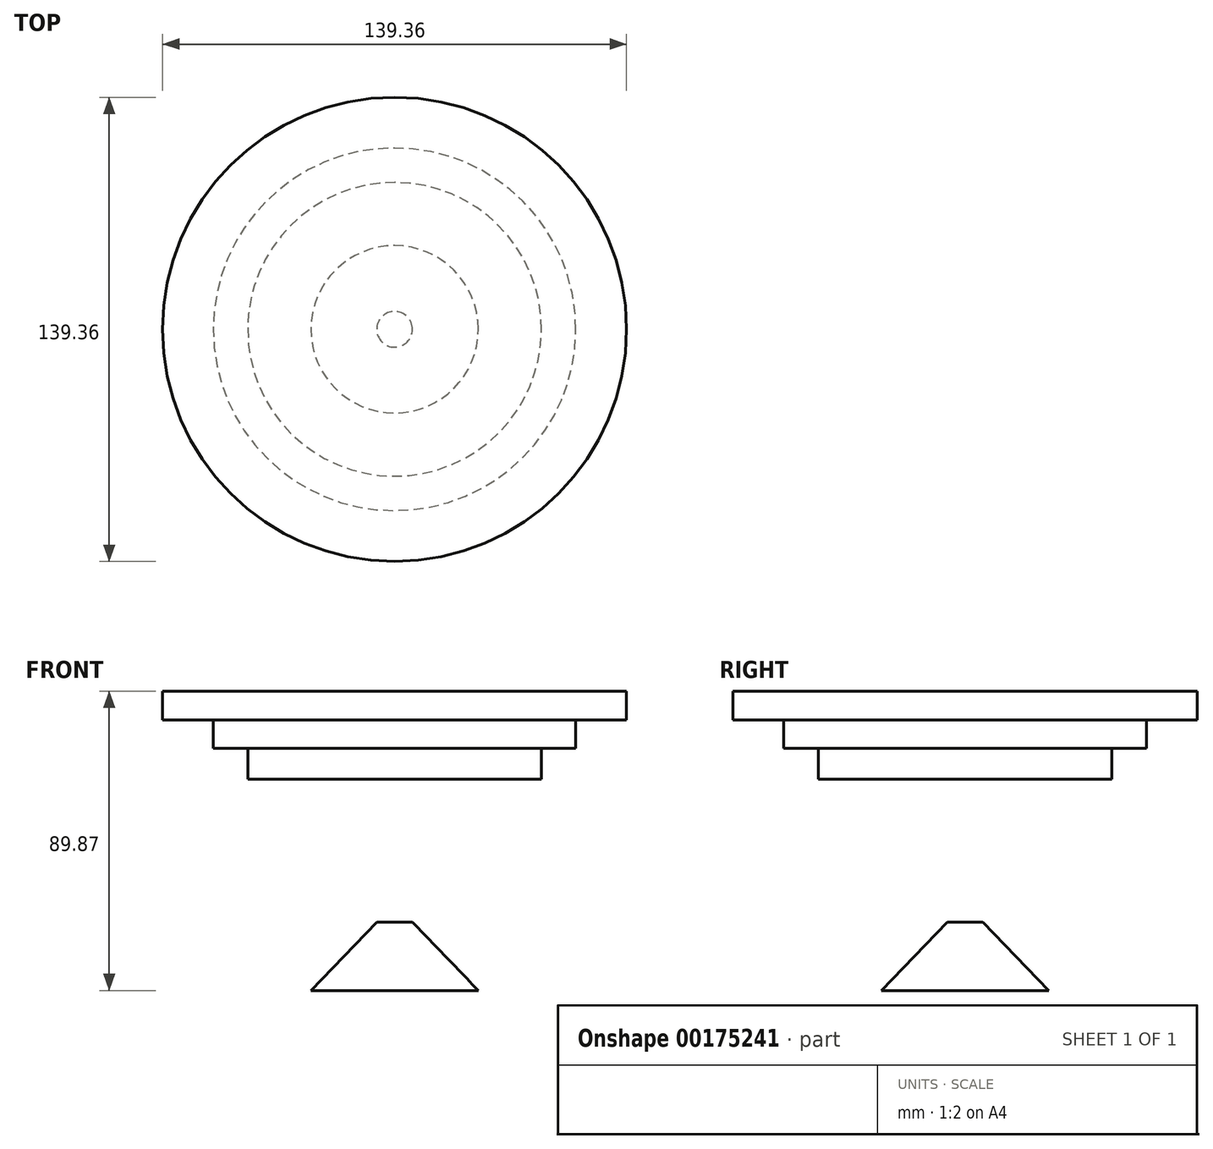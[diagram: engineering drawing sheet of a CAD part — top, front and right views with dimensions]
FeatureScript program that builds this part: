
annotation { "Feature Type Name" : "Feature", "Feature Type Description" : "" }
export const myFeature = defineFeature(function(context is Context, id is Id, definition is map)
    precondition{}
    {
        {
            var Q0;
            Q0=qCreatedBy(makeId("Front.planeOp"),FACE);
            var sketch = newSketch(context, id + "F0", { "sketchPlane" : qUnion([Q0])});
            skLineSegment(sketch, "E0", {"start": v(0, 69.58) * mm, "end": v(0, -55.57) * mm, "construction": true});
            skLineSegment(sketch, "E1", {"start": v(0, 40.38) * mm, "end": v(0, 31.14) * mm});
            skLineSegment(sketch, "E2", {"start": v(0, 31.14) * mm, "end": v(44.1, 31.14) * mm});
            skLineSegment(sketch, "E3", {"start": v(44.1, 31.14) * mm, "end": v(44.1, 40.38) * mm});
            skLineSegment(sketch, "E4.bottom", {"start": v(0, 31.14) * mm, "end": v(38.14, 31.14) * mm});
            skLineSegment(sketch, "E4.top", {"start": v(0, 22.5) * mm, "end": v(38.14, 22.5) * mm});
            skLineSegment(sketch, "E4.left", {"start": v(0, 31.14) * mm, "end": v(0, 22.5) * mm});
            skLineSegment(sketch, "E4.right", {"start": v(38.14, 31.14) * mm, "end": v(38.14, 22.5) * mm});
            skLineSegment(sketch, "E5.bottom", {"start": v(0, 22.5) * mm, "end": v(32.78, 22.5) * mm});
            skLineSegment(sketch, "E5.top", {"start": v(0, 15.94) * mm, "end": v(32.78, 15.94) * mm});
            skLineSegment(sketch, "E5.left", {"start": v(0, 22.5) * mm, "end": v(0, 15.94) * mm});
            skLineSegment(sketch, "E5.right", {"start": v(32.78, 22.5) * mm, "end": v(32.78, 15.94) * mm});
            skLineSegment(sketch, "E6.bottom", {"start": v(0, 15.94) * mm, "end": v(27.12, 15.94) * mm});
            skLineSegment(sketch, "E6.top", {"start": v(0, 9.98) * mm, "end": v(27.12, 9.98) * mm});
            skLineSegment(sketch, "E6.left", {"start": v(0, 15.94) * mm, "end": v(0, 9.98) * mm});
            skLineSegment(sketch, "E6.right", {"start": v(27.12, 15.94) * mm, "end": v(27.12, 9.98) * mm});
            skLineSegment(sketch, "E7.bottom", {"start": v(0, 9.98) * mm, "end": v(20.56, 9.98) * mm});
            skLineSegment(sketch, "E7.top", {"start": v(0, 4.62) * mm, "end": v(20.56, 4.62) * mm});
            skLineSegment(sketch, "E7.left", {"start": v(0, 9.98) * mm, "end": v(0, 4.62) * mm});
            skLineSegment(sketch, "E7.right", {"start": v(20.56, 9.98) * mm, "end": v(20.56, 4.62) * mm});
            skLineSegment(sketch, "E8.bottom", {"start": v(0, 4.62) * mm, "end": v(14.6, 4.62) * mm});
            skLineSegment(sketch, "E8.top", {"start": v(0, -2.53) * mm, "end": v(14.6, -2.53) * mm});
            skLineSegment(sketch, "E8.left", {"start": v(0, 4.62) * mm, "end": v(0, -2.53) * mm});
            skLineSegment(sketch, "E8.right", {"start": v(14.6, 4.62) * mm, "end": v(14.6, -2.53) * mm});
            skLineSegment(sketch, "E9.bottom", {"start": v(0, -2.53) * mm, "end": v(11.03, -2.53) * mm});
            skLineSegment(sketch, "E9.top", {"start": v(0, -6.7) * mm, "end": v(11.03, -6.7) * mm});
            skLineSegment(sketch, "E9.left", {"start": v(0, -2.53) * mm, "end": v(0, -6.7) * mm});
            skLineSegment(sketch, "E9.right", {"start": v(11.03, -2.53) * mm, "end": v(11.03, -6.7) * mm});
            skLineSegment(sketch, "E10.bottom", {"start": v(0, -6.7) * mm, "end": v(5.36, -6.7) * mm});
            skLineSegment(sketch, "E10.top", {"start": v(0, -11.77) * mm, "end": v(5.36, -11.77) * mm});
            skLineSegment(sketch, "E10.left", {"start": v(0, -6.7) * mm, "end": v(0, -11.77) * mm});
            skLineSegment(sketch, "E10.right", {"start": v(5.36, -6.7) * mm, "end": v(5.36, -11.77) * mm});
            skLineSegment(sketch, "E11.bottom", {"start": v(0, 40.38) * mm, "end": v(54.44, 40.38) * mm});
            skLineSegment(sketch, "E11.top", {"start": v(0, 48.88) * mm, "end": v(54.44, 48.88) * mm});
            skLineSegment(sketch, "E11.left", {"start": v(0, 40.38) * mm, "end": v(0, 48.88) * mm});
            skLineSegment(sketch, "E11.right", {"start": v(54.44, 40.38) * mm, "end": v(54.44, 48.88) * mm});
            skLineSegment(sketch, "E12.bottom", {"start": v(0, 48.88) * mm, "end": v(69.68, 48.88) * mm});
            skLineSegment(sketch, "E12.top", {"start": v(0, 57.56) * mm, "end": v(69.68, 57.56) * mm});
            skLineSegment(sketch, "E12.left", {"start": v(0, 48.88) * mm, "end": v(0, 57.56) * mm});
            skLineSegment(sketch, "E12.right", {"start": v(69.68, 48.88) * mm, "end": v(69.68, 57.56) * mm});
            skLineSegment(sketch, "E13", {"start": v(0, -11.77) * mm, "end": v(0, -32.3) * mm});
            skLineSegment(sketch, "E14", {"start": v(0, -32.3) * mm, "end": v(25.13, -32.3) * mm});
            skLineSegment(sketch, "E15", {"start": v(25.13, -32.3) * mm, "end": v(5.36, -11.77) * mm});
            skLineSegment(sketch, "E16", {"start": v(5.36, -11.77) * mm, "end": v(12.56, -32.3) * mm});
            skSolve(sketch);
        }
        {
            var Q0;
            Q0=makeQuery(id+"F0.imprint","IMPRINT",FACE,{"disambiguationData":[TD([[makeQuery(id+"F0.imprint","IMPRINT",EDGE,{"derivedFrom":sQuery(id+"F0.wireOp",EDGE,"E12.top")}),-1.0]])]});
            var Q1;
            {var subQ1=sQuery(id+"F0.wireOp",EDGE,"E11.left");Q1=makeQuery(id+"F0.imprint","IMPRINT",FACE,{"disambiguationData":[TD([[makeQuery(id+"F0.imprint","IMPRINT",EDGE,{"derivedFrom":subQ1}),-1.0]])]});}
            var Q2;
            {var subQ1=sQuery(id+"F0.wireOp",EDGE,"E1");Q2=makeQuery(id+"F0.imprint","IMPRINT",FACE,{"disambiguationData":[TD([[makeQuery(id+"F0.imprint","IMPRINT",EDGE,{"derivedFrom":subQ1}),1.0]])]});}
            var Q3;
            Q3=makeQuery(id+"F0.imprint","IMPRINT",FACE,{"disambiguationData":[TD([[makeQuery(id+"F0.imprint","IMPRINT",EDGE,{"derivedFrom":sQuery(id+"F0.wireOp",EDGE,"E4.bottom")}),-1.0]])]});
            var Q4;
            Q4=makeQuery(id+"F0.imprint","IMPRINT",FACE,{"disambiguationData":[TD([[makeQuery(id+"F0.imprint","IMPRINT",EDGE,{"derivedFrom":sQuery(id+"F0.wireOp",EDGE,"E5.bottom")}),-1.0]])]});
            var Q5;
            Q5=makeQuery(id+"F0.imprint","IMPRINT",FACE,{"disambiguationData":[TD([[makeQuery(id+"F0.imprint","IMPRINT",EDGE,{"derivedFrom":sQuery(id+"F0.wireOp",EDGE,"E6.bottom")}),-1.0]])]});
            var Q6;
            Q6=makeQuery(id+"F0.imprint","IMPRINT",FACE,{"disambiguationData":[TD([[makeQuery(id+"F0.imprint","IMPRINT",EDGE,{"derivedFrom":sQuery(id+"F0.wireOp",EDGE,"E7.bottom")}),-1.0]])]});
            var Q7;
            Q7=makeQuery(id+"F0.imprint","IMPRINT",FACE,{"disambiguationData":[TD([[makeQuery(id+"F0.imprint","IMPRINT",EDGE,{"derivedFrom":sQuery(id+"F0.wireOp",EDGE,"E8.bottom")}),-1.0]])]});
            var Q8;
            Q8=makeQuery(id+"F0.imprint","IMPRINT",FACE,{"disambiguationData":[TD([[makeQuery(id+"F0.imprint","IMPRINT",EDGE,{"derivedFrom":sQuery(id+"F0.wireOp",EDGE,"E9.bottom")}),-1.0]])]});
            var Q9;
            Q9=makeQuery(id+"F0.imprint","IMPRINT",FACE,{"disambiguationData":[TD([[makeQuery(id+"F0.imprint","IMPRINT",EDGE,{"derivedFrom":sQuery(id+"F0.wireOp",EDGE,"E10.bottom")}),-1.0]])]});
            var Q10;
            Q10=makeQuery(id+"F0.imprint","IMPRINT",FACE,{"disambiguationData":[TD([[makeQuery(id+"F0.imprint","IMPRINT",EDGE,{"derivedFrom":sQuery(id+"F0.wireOp",EDGE,"E10.top")}),-1.0]])]});
            var Q11;
            {var subQ0=sQuery(id+"F0.wireOp",EDGE,"E15");Q11=makeQuery(id+"F0.imprint","IMPRINT",FACE,{"disambiguationData":[TD([[makeQuery(id+"F0.imprint","IMPRINT",EDGE,{"derivedFrom":subQ0}),1.0]])]});}
            var Q12;
            Q12=sQuery(id+"F0.wireOp",EDGE,"E0");
            revolve(context, id + "F1", {"entities" : qUnion([Q0, Q1, Q2, Q3, Q4, Q5, Q6, Q7, Q8, Q9, Q10, Q11]), "axis" : qUnion([Q12]), "revolveType" : RevolveType.FULL});
        }
    });
